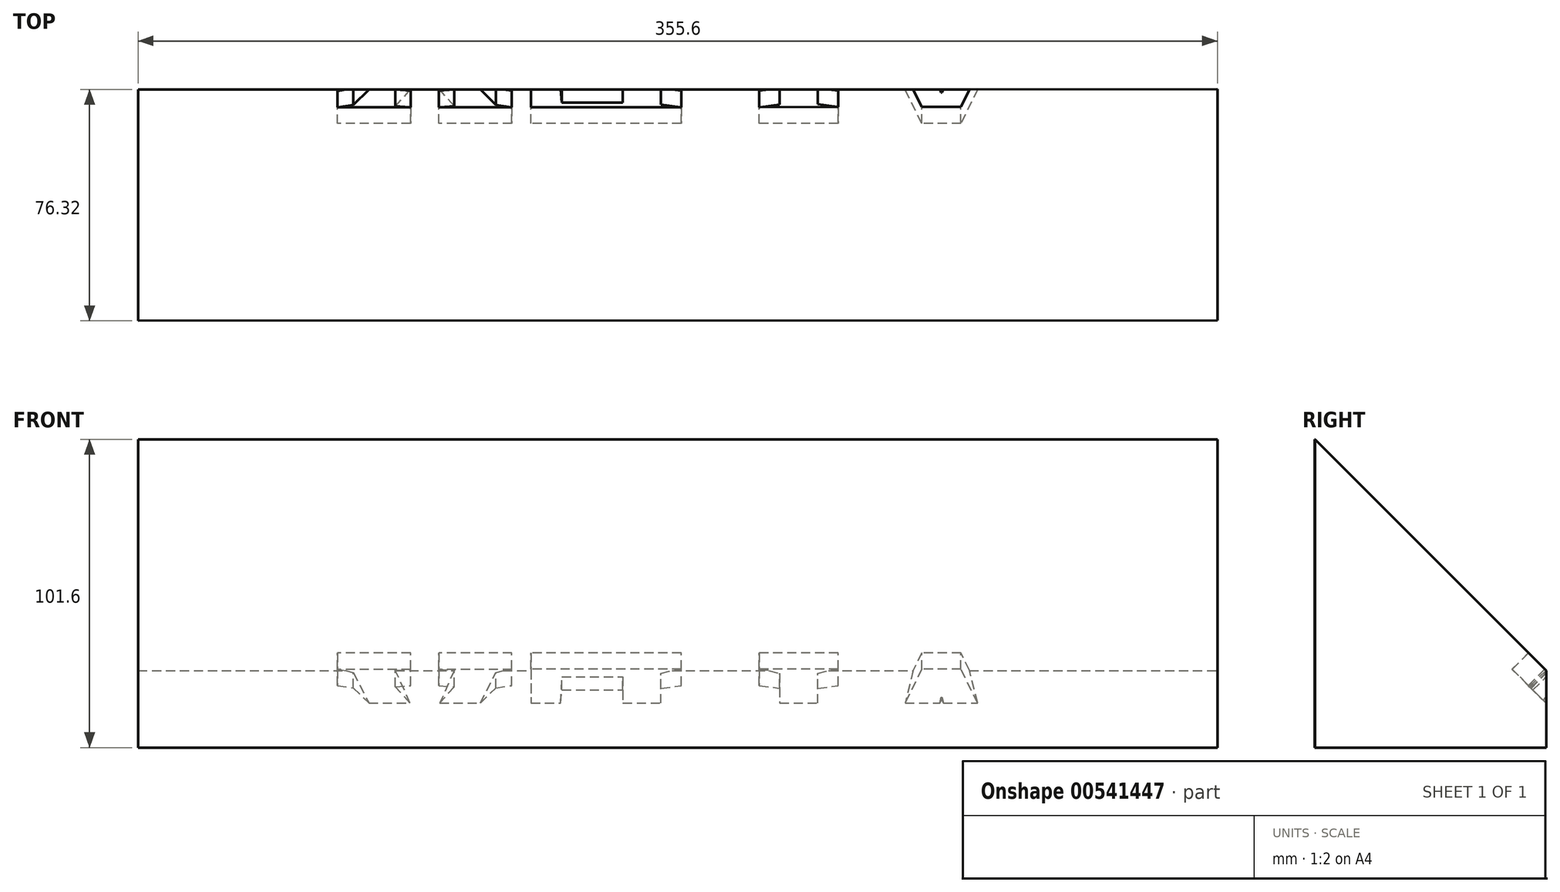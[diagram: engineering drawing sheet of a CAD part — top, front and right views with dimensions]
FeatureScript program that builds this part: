
annotation { "Feature Type Name" : "Feature", "Feature Type Description" : "" }
export const myFeature = defineFeature(function(context is Context, id is Id, definition is map)
    precondition{}
    {
        {
            var Q0;
            Q0=qCreatedBy(makeId("Top.planeOp"),FACE);
            var sketch = newSketch(context, id + "F0", { "sketchPlane" : qUnion([Q0])});
            skLineSegment(sketch, "E0.left", {"start": v(177.8, -38.04) * mm, "end": v(177.8, 38.16) * mm});
            skLineSegment(sketch, "E0.right", {"start": v(-177.8, -38.16) * mm, "end": v(-177.8, 38.04) * mm});
            skLineSegment(sketch, "E1", {"start": v(-177.8, 38.04) * mm, "end": v(177.8, 38.16) * mm});
            skLineSegment(sketch, "E2", {"start": v(-177.8, -38.16) * mm, "end": v(177.8, -38.04) * mm});
            skLineSegment(sketch, "E3", {"start": v(0, 38.1) * mm, "end": v(0, -38.1) * mm, "construction": true});
            skPoint(sketch, "E4", {"position": v(0, 0) * mm});
            skSolve(sketch);
        }
        {
            var Q0;
            {var subQ0=sQuery(id+"F0.wireOp",EDGE,"E0.left");Q0=makeQuery(id+"F0.imprint","IMPRINT",FACE,{"disambiguationData":[TD([[makeQuery(id+"F0.imprint","IMPRINT",EDGE,{"derivedFrom":subQ0}),1.0]])]});}
            var Q1;
            {var subQ0=sQuery(id+"F0.wireOp",EDGE,"f78de060-f92b-4e90-a891-c1896b122fa7.2");var subQ1=sQuery(id+"F0.wireOp",EDGE,"f78de060-f92b-4e90-a891-c1896b122fa7.1");var subQ2=makeQuery(id+"F0.imprint","INTERSECT",VERTEX,{"derivedFrom":[subQ1,subQ0]});Q1=makeQuery(id+"F0.imprint","IMPRINT",FACE,{"disambiguationData":[TD([[makeQuery(id+"F0.imprint","IMPRINT",EDGE,{"disambiguationData":[TD([[subQ2,1.0]])],"derivedFrom":subQ1}),-1.0]])]});}
            extrude(context, id + "F1", {"entities" : qUnion([Q0, Q1]), "depth" : 101.6 * mm, "offsetDistance" : 25.4 * mm});
        }
        {
            var Q0;
            Q0=makeQuery(id+"F1.opExtrude","CAP_EDGE",EDGE,{"disambiguationData":[OSD([sQuery(id+"F0.wireOp",EDGE,"E1")])],"isStart":false});
            chamfer(context, id + "F2", {"entities" : qUnion([Q0]), "width" : 76.2 * mm, "tangentPropagation" : true});
        }
        {
            var Q0;
            Q0=makeQuery(id+"F2.opChamfer","BLEND_FACE",FACE,{"disambiguationData":[OSD([sQuery(id+"F0.wireOp",EDGE,"E1")])]});
            cPlane(context, id + "F3", {"entities" : qUnion([Q0]), "cplaneType" : CPlaneType.OFFSET, "offset" : 0 * mm, "width" : 152.4 * mm, "height" : 152.4 * mm});
        }
        {
            var Q0;
            Q0=qCreatedBy(id+"F3.planeOp",FACE);
            var sketch = newSketch(context, id + "F4", { "sketchPlane" : qUnion([Q0])});
            skPoint(sketch, "E5", {"position": v(467.4, -117.33) * mm});
            skText(sketch, "E6", { "text": "ALEX", "fontName": "RobotoSlab-Bold.ttf"});
            skPoint(sketch, "E7", {"position": v(0, -31.75) * mm});
            const initialGuessF4  = {"E6": [-0.11861, -0.0635, 1, 0, 0.0635]};
            skSetInitialGuess(sketch, initialGuessF4);
            skSolve(sketch);
        }
        {
            var Q0;
            Q0=qSketchRegion(id+"F4",true);
            extrude(context, id + "F5", {"entities" : qUnion([Q0]), "operationType" : NewBodyOperationType.REMOVE, "oppositeDirection" : true, "depth" : 7.62 * mm, "offsetDistance" : 25.4 * mm});
        }
    });
